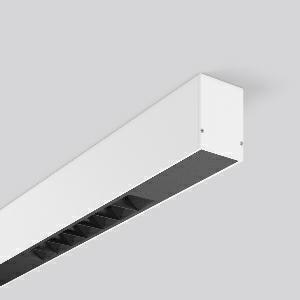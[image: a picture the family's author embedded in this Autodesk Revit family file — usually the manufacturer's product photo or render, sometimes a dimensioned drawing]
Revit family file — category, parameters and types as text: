
# Revit family: less_is_more_beamline_312485_002_1_76_1420
name_source: partatom
category: Lighting Fixtures
units: mm (PartAtom-declared; Revit-internal decimal feet)

## family parameters
Cut with Voids When Loaded = No
Host = Face
Light Source = No
Part Type = Normal
Room Calculation Point = No
Round Connector Dimension = Use Diameter
Shared = No

## types (1)
- LESS IS MORE BEAMLINE (1 x LED Modul 940, 1100 lm, 4000)
    Apparent Load = 23 VA
    CIE Flux Codes = 100 100 100 100 100
    Color Rendering = 92
    Color Temperature = 4000
    Default Elevation = 1800 mm
    Description = Series: LESS IS MORE BEAMLINE
Linear ceiling and wall luminaire for aesthetically sophisticated lighting. Luminaire with two LED light units. Housing: extruded aluminium profile, powder-coated. End cap aluminium powder-coated. LED light unit with MRS technology: Mini-Reflector-System made of metallised thermoplastic with prismatic black glare-suppressing frame for pleasant glare-free light (RUG < 10). Each LED light unit has 7 reflector elements. Wide beam light distribution. LED unit with integrated converter interchangeable and removable. Suitable for through-wiring. 
Colour: traffic white, matt (RAL 9016)
Length: 1127 mm
Width: 57 mm
Height: 75 mm
Lamp: LED
Socket: without socket
Colour temperature: 4000K
Colour rendering index (CRI): 90
System power: 23 W
Rated luminous flux: 2200 lm
Luminous efficiency: 96 lm/W
Control gear: Converter, dimmable, DALI
Protection class: I
Type of protection: IP 20
    Height = 75 mm
    Lamp = 1 x LED Modul 940
    Lamp Light Flux = 1100 lm
    Lamp count = 1
    Length = 1127 mm
    Lifetime = 50000 h
    Luminous efficacy = 96 lm/W
    Manufacturer = RZB
    ModVariant = No
    Model = 312485.002.1.76
    Mounting Place = Ceiling, Wall
    Mounting Type = Surface mounted
    Number of Poles = 1
    OnlyDefault = Yes
    Power Factor = 1
    Product Name = LESS IS MORE BEAMLINE
    Product group = Surface mounted LED linear luminaires
    ProductGroupID = 307
    Protection Class = Protection class I
    Protection Degree = IP 20
    RLX_Detail_Level = 1
    RLX_Emergency_Light_Flux = 0 lm
    RLX_Emergency_Type = 0
    RLX_Emergency_Type_DB = No
    RlxData = <blob elided: 26913 chars, md5=4ff59235>
    Socket = socket
    Standby Power = 0 W
    System Light Flux = 2200 lm
    System Power = 23 W
    Type Comments = Product without accessories
    Type Image = 312483.002.jpg
    URL = http://relux.com
    VarID = ---
    Voltage = 230 V
    Voltage Range = 220-240 V
    Weight = 0.00 kg
    Width = 57 mm

## geometry (parser evidence)
native form markers: Blend x4, Sweep x17
no freeform markers — native parametric forms only
